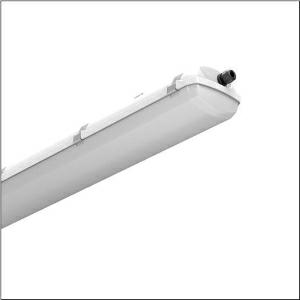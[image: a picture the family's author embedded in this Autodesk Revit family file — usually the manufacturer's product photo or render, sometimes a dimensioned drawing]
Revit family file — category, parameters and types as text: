
# Revit family: monsun_ex_51fxa27l840a
name_source: partatom
category: Lighting Fixtures
units: mm (PartAtom-declared; Revit-internal decimal feet)

## family parameters
Cut with Voids When Loaded = No
Host = Face
Light Source = No
Part Type = Normal
Room Calculation Point = No
Round Connector Dimension = Use Diameter
Shared = No

## types (1)
- Monsun Ex (1 x LED, 4650 lm, 33 W, 6500K)
    Apparent Load = 33 VA
    CIE Flux Codes = 46 76 94 98 100
    Color Rendering = 80
    Color Temperature = 6500K
    Default Elevation = 1800 mm
    Description = Monsun Ex, damp-proof luminaire, primary optical cover: cover, of PC, UV-stabilised, opal, light emission: direct distribution, primary light characteristic: symmetric, installation type: surface-mounted, LED, rated luminous flux: 4.650lm, luminous efficacy: 141lm/W, light colour: 860, colour temperature: 6000K, control gear: ON/OFF, with terminal, 3-pole, max. 2.5mm², through-wiring: 5x 2.5mm², mains connection: 220..250V, AC, 50/60Hz, rated input power: 33W, housing, of PC, light grey (RAL 7035), incl. 2x Ex cable gland M20 for cable diameter 7..12mm with sealing, incl. 1x Ex locking screw M20 with sealing, length: 1.280mm, width: 155mm, height: 105mm, clip for enclosure, of stainless steel, protection rating (complete): IP66, insulation class (complete): insulation class I (protective earthing), certification: CE, explosion class: zone 1,21 II 2G Ex eb mb op is IIC T4 Gb, II 2D Ex tb op is IIIC T67°C Db, impact resistance: IK10, permissible operating ambient temperature: -20..+40°C, contact your sales advisor before using the luminaires in applications with unclear chemical exposure, large temperature fluctuations or condensation-forming humidity, packaging unit: 1 piece
    Height = 105 mm
    Lamp = 1 x LED
    Lamp Light Flux = 4650 lm
    Lamp Power = 33 W
    Lamp count = 1
    Length = 1280 mm
    Luminous efficacy = 141 lm/W
    Manufacturer = Siteco
    ModVariant = No
    Model = 51FXA27L840A
    Mounting Place = Ceiling
    Mounting Type = Surface mounted
    Number of Poles = 1
    OnlyDefault = Yes
    Power Factor = 1
    Product Name = Monsun Ex
    Product group = damp-proof luminaire
    ProductGroupID = 300
    Protection Class = Protection class I
    Protection Degree = IP 66
    RLX_Detail_Level = 1
    RLX_Emergency_Light_Flux = 0 lm
    RLX_Emergency_Type = 0
    RLX_Emergency_Type_DB = No
    RlxData = <blob elided: 41521 chars, md5=598d95f2>
    Socket = socket
    Standby Power = 0 W
    System Light Flux = 4650 lm
    System Power = 33 W
    Type Comments = Product without accessories
    Type Image = l_1258882.jpg
    URL = http://relux.com
    VarID = ---
    Voltage = 0 V
    Weight = 0.00 kg
    Width = 155 mm

## geometry (parser evidence)
native form markers: Blend x4, Sweep x10
no freeform markers — native parametric forms only
